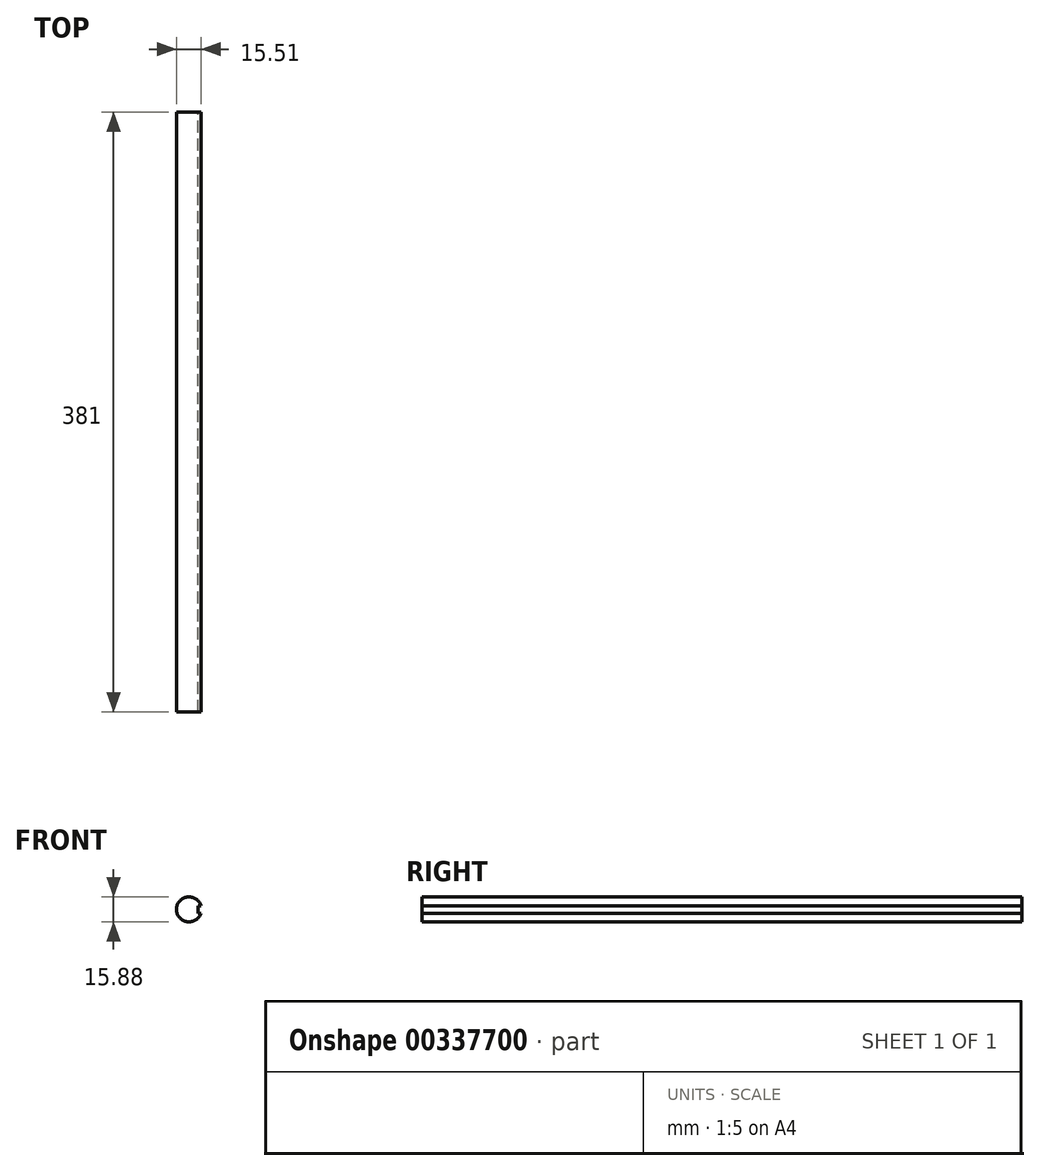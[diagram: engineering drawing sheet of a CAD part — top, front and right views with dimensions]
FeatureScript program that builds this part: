
annotation { "Feature Type Name" : "Feature", "Feature Type Description" : "" }
export const myFeature = defineFeature(function(context is Context, id is Id, definition is map)
    precondition{}
    {
        {
            var Q0;
            Q0=qCreatedBy(makeId("Front.planeOp"),FACE);
            var sketch = newSketch(context, id + "F0", { "sketchPlane" : qUnion([Q0])});
            skCircle(sketch, "E0", {"center": v(0, 0) * mm, "radius": 7.94 * mm});
            skLineSegment(sketch, "E1.bottom", {"start": v(5.76, 2.38) * mm, "end": v(10.11, 2.38) * mm});
            skLineSegment(sketch, "E1.top", {"start": v(5.76, -2.38) * mm, "end": v(10.11, -2.38) * mm});
            skLineSegment(sketch, "E1.left", {"start": v(5.76, 2.38) * mm, "end": v(5.76, -2.38) * mm});
            skLineSegment(sketch, "E1.right", {"start": v(10.11, 2.38) * mm, "end": v(10.11, -2.38) * mm});
            skLineSegment(sketch, "E2", {"start": v(7.94, 2.38) * mm, "end": v(7.94, 0) * mm});
            skLineSegment(sketch, "E3", {"start": v(7.94, 0) * mm, "end": v(7.94, -2.38) * mm});
            skSolve(sketch);
        }
        {
            var Q0;
            {var subQ5=sQuery(id+"F0.wireOp",EDGE,"E1.left");Q0=makeQuery(id+"F0.imprint","IMPRINT",FACE,{"disambiguationData":[TD([[makeQuery(id+"F0.imprint","IMPRINT",EDGE,{"derivedFrom":subQ5}),-1.0]])]});}
            extrude(context, id + "F1", {"entities" : qUnion([Q0]), "depth" : 381 * mm});
        }
    });
